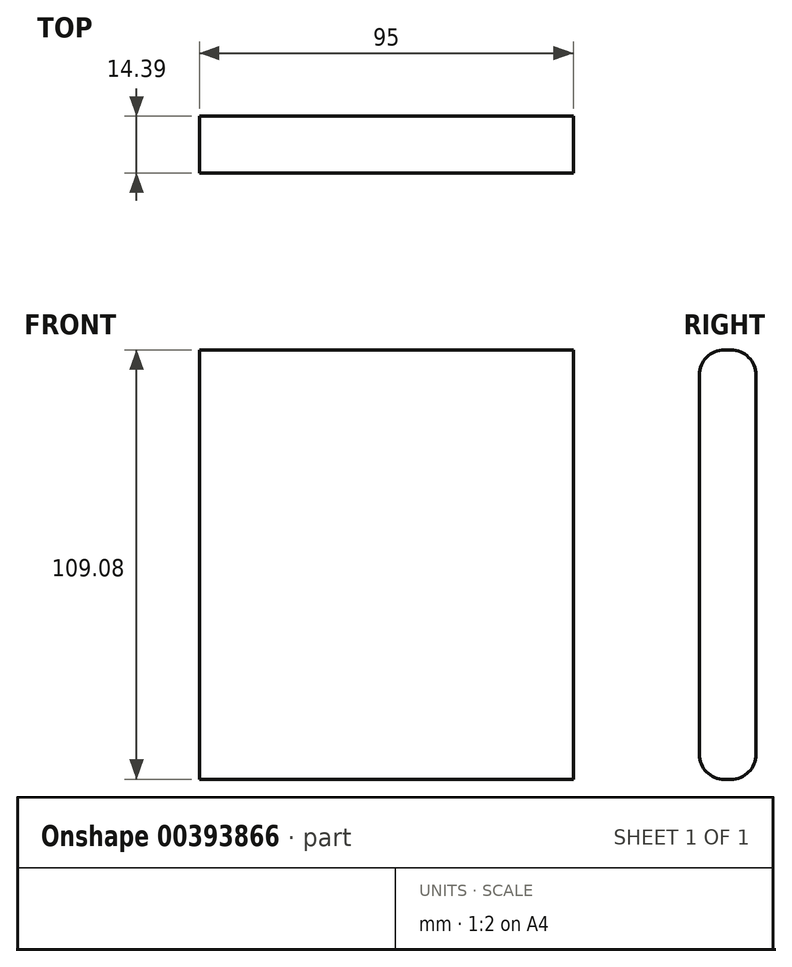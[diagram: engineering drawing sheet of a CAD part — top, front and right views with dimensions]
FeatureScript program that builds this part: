
annotation { "Feature Type Name" : "Feature", "Feature Type Description" : "" }
export const myFeature = defineFeature(function(context is Context, id is Id, definition is map)
    precondition{}
    {
        {
            var Q0;
            Q0=qCreatedBy(makeId("Right.planeOp"),FACE);
            var sketch = newSketch(context, id + "F0", { "sketchPlane" : qUnion([Q0])});
            skLineSegment(sketch, "E0.bottom", {"start": v(6.35, 40.87) * mm, "end": v(8.04, 40.87) * mm});
            skLineSegment(sketch, "E0.top", {"start": v(6.35, -68.2) * mm, "end": v(8.04, -68.2) * mm});
            skLineSegment(sketch, "E0.left", {"start": v(0, 34.52) * mm, "end": v(0, -61.86) * mm});
            skLineSegment(sketch, "E0.right", {"start": v(14.4, 34.52) * mm, "end": v(14.4, -61.86) * mm});
            skPoint(sketch, "E1.visualSharp", {"position": v(0, 40.87) * mm});
            skArc(sketch, "E1.filletArc", {"start": v(6.35, 40.87) * mm, "mid": v(1.86, 39) * mm, "end": v(0, 34.52) * mm});
            skPoint(sketch, "E2.visualSharp", {"position": v(0, -68.2) * mm});
            skArc(sketch, "E2.filletArc", {"start": v(0, -61.86) * mm, "mid": v(1.86, -66.35) * mm, "end": v(6.35, -68.2) * mm});
            skPoint(sketch, "E3.visualSharp", {"position": v(14.4, -68.2) * mm});
            skArc(sketch, "E3.filletArc", {"start": v(8.04, -68.2) * mm, "mid": v(12.53, -66.35) * mm, "end": v(14.4, -61.86) * mm});
            skPoint(sketch, "E4.visualSharp", {"position": v(14.4, 40.87) * mm});
            skArc(sketch, "E4.filletArc", {"start": v(14.4, 34.52) * mm, "mid": v(12.53, 39) * mm, "end": v(8.04, 40.87) * mm});
            skSolve(sketch);
        }
        {
            var Q0;
            Q0 = qSketchRegion(id + "F0", true);
            extrude(context, id + "F1", {"entities" : qUnion([Q0]), "depth" : 95 * mm});
        }
    });
